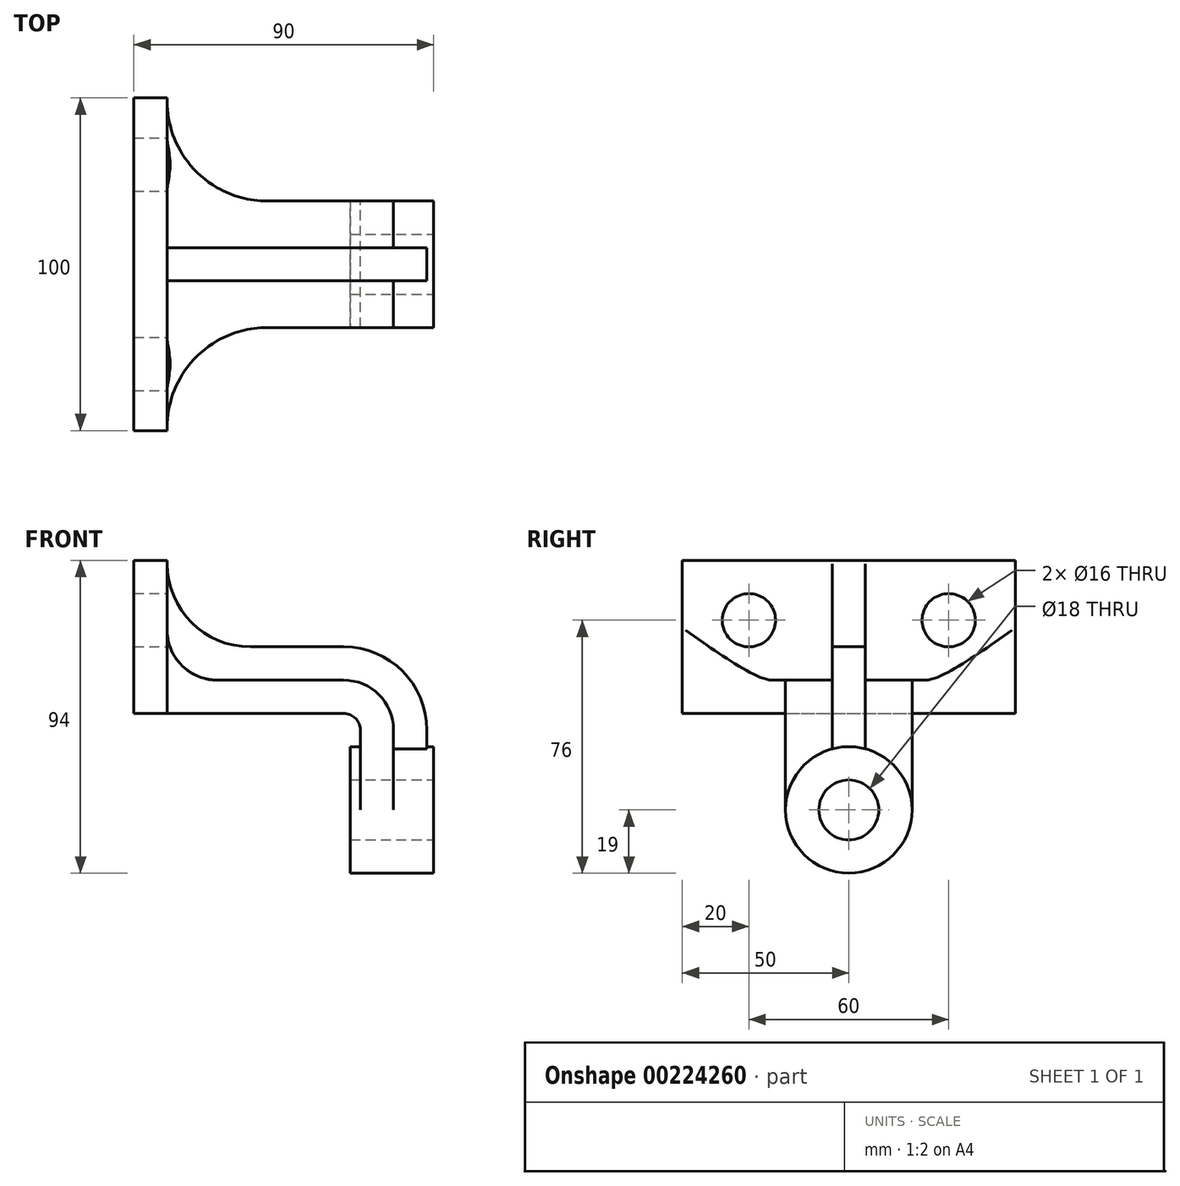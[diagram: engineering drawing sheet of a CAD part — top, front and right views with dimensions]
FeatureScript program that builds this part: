
annotation { "Feature Type Name" : "Feature", "Feature Type Description" : "" }
export const myFeature = defineFeature(function(context is Context, id is Id, definition is map)
    precondition{}
    {
        {
            var Q0;
            Q0=qCreatedBy(makeId("Front.planeOp"),FACE);
            var sketch = newSketch(context, id + "F0", { "sketchPlane" : qUnion([Q0])});
            skLineSegment(sketch, "E0", {"start": v(0, 0) * mm, "end": v(0, 46) * mm});
            skLineSegment(sketch, "E1", {"start": v(0, 46) * mm, "end": v(10, 46) * mm});
            skLineSegment(sketch, "E2", {"start": v(10, 46) * mm, "end": v(10, 0) * mm});
            skLineSegment(sketch, "E3", {"start": v(10, 0) * mm, "end": v(0, 0) * mm});
            skLineSegment(sketch, "E4", {"start": v(0, 0) * mm, "end": v(0, 10) * mm});
            skLineSegment(sketch, "E5", {"start": v(0, 10) * mm, "end": v(78, 10) * mm});
            skLineSegment(sketch, "E6", {"start": v(78, 10) * mm, "end": v(78, 0) * mm});
            skLineSegment(sketch, "E7", {"start": v(78, 0) * mm, "end": v(0, 0) * mm});
            skLineSegment(sketch, "E8", {"start": v(78, 10) * mm, "end": v(78, -48) * mm});
            skLineSegment(sketch, "E9", {"start": v(78, -48) * mm, "end": v(68, -48) * mm});
            skLineSegment(sketch, "E10", {"start": v(68, -48) * mm, "end": v(68, 10) * mm});
            skSolve(sketch);
        }
        {
            var Q0;
            {var subQ0=sQuery(id+"F0.wireOp",EDGE,"E0");Q0=makeQuery(id+"F0.imprint","IMPRINT",FACE,{"disambiguationData":[TD([[makeQuery(id+"F0.imprint","IMPRINT",EDGE,{"derivedFrom":subQ0}),-1.0]])]});}
            var Q1;
            {var subQ5=sQuery(id+"F0.wireOp",EDGE,"E4");Q1=makeQuery(id+"F0.imprint","IMPRINT",FACE,{"disambiguationData":[TD([[makeQuery(id+"F0.imprint","IMPRINT",EDGE,{"derivedFrom":subQ5}),-1.0]])]});}
            var Q2;
            {var subQ0=sQuery(id+"F0.wireOp",EDGE,"E7");var subQ1=sQuery(id+"F0.wireOp",EDGE,"E2");var subQ2=makeQuery(id+"F0.imprint","INTERSECT",VERTEX,{"derivedFrom":[subQ1,subQ0]});Q2=makeQuery(id+"F0.imprint","IMPRINT",FACE,{"disambiguationData":[TD([[makeQuery(id+"F0.imprint","IMPRINT",EDGE,{"disambiguationData":[TD([[subQ2,1.0]])],"derivedFrom":subQ1}),1.0]])]});}
            var Q3;
            {var subQ0=sQuery(id+"F0.wireOp",EDGE,"E8");var subQ1=sQuery(id+"F0.wireOp",EDGE,"E5");var subQ2=makeQuery(id+"F0.imprint","INTERSECT",VERTEX,{"derivedFrom":[subQ1,subQ0]});Q3=makeQuery(id+"F0.imprint","IMPRINT",FACE,{"disambiguationData":[TD([[makeQuery(id+"F0.imprint","IMPRINT",EDGE,{"disambiguationData":[TD([[subQ2,1.0]])],"derivedFrom":subQ1}),-1.0]])]});}
            var Q4;
            {var subQ5=sQuery(id+"F0.wireOp",EDGE,"E9");Q4=makeQuery(id+"F0.imprint","IMPRINT",FACE,{"disambiguationData":[TD([[makeQuery(id+"F0.imprint","IMPRINT",EDGE,{"derivedFrom":subQ5}),-1.0]])]});}
            extrude(context, id + "F1", {"entities" : qUnion([Q0, Q1, Q2, Q3, Q4]), "endBound" : BoundingType.SYMMETRIC, "depth" : 100 * mm});
        }
        {
            var Q0;
            Q0=makeQuery(id+"F1.opExtrude","SWEPT_FACE",FACE,{"disambiguationData":[OSD([sQuery(id+"F0.wireOp",EDGE,"E2")])]});
            var sketch = newSketch(context, id + "F2", { "sketchPlane" : qUnion([Q0])});
            skCircle(sketch, "E11", {"center": v(-30, 28) * mm, "radius": 8 * mm});
            skCircle(sketch, "E12", {"center": v(30, 28) * mm, "radius": 8 * mm});
            skSolve(sketch);
        }
        {
            var Q0;
            Q0=makeQuery(id+"F1.opExtrude","SWEPT_FACE",FACE,{"disambiguationData":[OSD([sQuery(id+"F0.wireOp",EDGE,"E5")])]});
            var sketch = newSketch(context, id + "F3", { "sketchPlane" : qUnion([Q0])});
            skLineSegment(sketch, "E13", {"start": v(10, -19) * mm, "end": v(78, -19) * mm});
            skLineSegment(sketch, "E14", {"start": v(10, 19) * mm, "end": v(78, 19) * mm});
            skArc(sketch, "E15", {"start": v(40, -19) * mm, "mid": v(18.79, -27.79) * mm, "end": v(10, -49) * mm});
            skArc(sketch, "E16", {"start": v(10, 49) * mm, "mid": v(18.79, 27.79) * mm, "end": v(40, 19) * mm});
            skLineSegment(sketch, "E17.0", {"start": v(10, -22) * mm, "end": v(10, -38) * mm});
            skLineSegment(sketch, "E18.0", {"start": v(10, 38) * mm, "end": v(10, 22) * mm});
            skLineSegment(sketch, "E19.0", {"start": v(10, -50) * mm, "end": v(10, 50) * mm});
            skSolve(sketch);
        }
        {
            var Q0;
            {var subQ3=sQuery(id+"F3.wireOp",EDGE,"E15");Q0=makeQuery(id+"F3.imprint","IMPRINT",FACE,{"disambiguationData":[TD([[makeQuery(id+"F3.imprint","IMPRINT",EDGE,{"derivedFrom":subQ3}),1.0]])]});}
            var Q1;
            {var subQ3=sQuery(id+"F3.wireOp",EDGE,"E16");Q1=makeQuery(id+"F3.imprint","IMPRINT",FACE,{"disambiguationData":[TD([[makeQuery(id+"F3.imprint","IMPRINT",EDGE,{"derivedFrom":subQ3}),1.0]])]});}
            extrude(context, id + "F4", {"entities" : qUnion([Q0, Q1]), "operationType" : NewBodyOperationType.REMOVE, "endBound" : BoundingType.THROUGH_ALL, "oppositeDirection" : true, "depth" : 25 * mm});
        }
        {
            var Q0;
            Q0=makeQuery(id+"F2.imprint","IMPRINT",FACE,{"disambiguationData":[TD([[makeQuery(id+"F2.imprint","IMPRINT",EDGE,{"derivedFrom":sQuery(id+"F2.wireOp",EDGE,"E12")}),1.0]])]});
            var Q1;
            Q1=makeQuery(id+"F2.imprint","IMPRINT",FACE,{"disambiguationData":[TD([[makeQuery(id+"F2.imprint","IMPRINT",EDGE,{"derivedFrom":sQuery(id+"F2.wireOp",EDGE,"E11")}),1.0]])]});
            extrude(context, id + "F5", {"entities" : qUnion([Q0, Q1]), "operationType" : NewBodyOperationType.REMOVE, "oppositeDirection" : true, "depth" : 25 * mm});
        }
        {
            var Q0;
            Q0=makeQuery(id+"F1.opExtrude","SWEPT_EDGE",EDGE,{"disambiguationData":[OSD([sQuery(id+"F0.wireOp",EDGE,"E5"),sQuery(id+"F0.wireOp",EDGE,"E8")])]});
            fillet(context, id + "F6", {"entities" : qUnion([Q0]), "radius" : 15 * mm, "tangentPropagation" : true, "allowEdgeOverflow" : false});
        }
        {
            var Q0;
            Q0=makeQuery(id+"F1.opExtrude","SWEPT_EDGE",EDGE,{"disambiguationData":[OSD([sQuery(id+"F0.wireOp",EDGE,"E7"),sQuery(id+"F0.wireOp",EDGE,"E10")])]});
            fillet(context, id + "F7", {"entities" : qUnion([Q0]), "radius" : 5 * mm, "tangentPropagation" : true, "allowEdgeOverflow" : false});
        }
        {
            var Q0;
            Q0=qCreatedBy(makeId("Front.planeOp"),FACE);
            var sketch = newSketch(context, id + "F8", { "sketchPlane" : qUnion([Q0])});
            skLineSegment(sketch, "E20.0", {"start": v(10, 46) * mm, "end": v(10, 0) * mm});
            skLineSegment(sketch, "E21", {"start": v(35, 20) * mm, "end": v(88, 20) * mm});
            skLineSegment(sketch, "E22", {"start": v(88, 20) * mm, "end": v(88, -48) * mm});
            skLineSegment(sketch, "E23", {"start": v(88, -48) * mm, "end": v(77.42, -48) * mm});
            skArc(sketch, "E24", {"start": v(10, 45) * mm, "mid": v(17.32, 27.32) * mm, "end": v(35, 20) * mm});
            skLineSegment(sketch, "E25.0.0", {"start": v(0, 0) * mm, "end": v(10, 0) * mm});
            skLineSegment(sketch, "E25.0.1", {"start": v(10, 0) * mm, "end": v(10, 46) * mm});
            skLineSegment(sketch, "E25.0.2", {"start": v(10, 46) * mm, "end": v(0, 46) * mm});
            skLineSegment(sketch, "E25.0.3", {"start": v(0, 46) * mm, "end": v(0, 0) * mm});
            skLineSegment(sketch, "E26.0", {"start": v(10, 10) * mm, "end": v(40, 10) * mm});
            skLineSegment(sketch, "E27.0", {"start": v(10, 10) * mm, "end": v(63, 10) * mm});
            skArc(sketch, "E28.0", {"start": v(78, -5) * mm, "mid": v(73.6, 5.6) * mm, "end": v(63, 10) * mm});
            skLineSegment(sketch, "E29.0", {"start": v(78, -48) * mm, "end": v(78, -5) * mm});
            skPoint(sketch, "E30.orphan", {"position": v(78, 10) * mm});
            skSolve(sketch);
        }
        {
            var Q0;
            Q0=makeQuery(id+"F8.imprint","IMPRINT",FACE,{"disambiguationData":[TD([[makeQuery(id+"F8.imprint","IMPRINT",EDGE,{"derivedFrom":sQuery(id+"F8.wireOp",EDGE,"E21")}),-1.0]])]});
            extrude(context, id + "F9", {"entities" : qUnion([Q0]), "operationType" : NewBodyOperationType.ADD, "endBound" : BoundingType.SYMMETRIC, "depth" : 10 * mm});
        }
        {
            var Q0;
            Q0=makeQuery(id+"F9.opExtrude","SWEPT_EDGE",EDGE,{"disambiguationData":[OSD([sQuery(id+"F8.wireOp",EDGE,"E21"),sQuery(id+"F8.wireOp",EDGE,"E22")])]});
            fillet(context, id + "F10", {"entities" : qUnion([Q0]), "radius" : 25 * mm, "tangentPropagation" : true, "allowEdgeOverflow" : false});
        }
        {
            var Q0;
            Q0=makeQuery(id+"F9.opExtrude","SWEPT_FACE",FACE,{"disambiguationData":[OSD([sQuery(id+"F8.wireOp",EDGE,"E22")])]});
            cPlane(context, id + "F11", {"entities" : qUnion([Q0]), "cplaneType" : CPlaneType.OFFSET, "offset" : 2 * mm, "width" : 150 * mm, "height" : 150 * mm});
        }
        {
            var Q0;
            Q0=qCreatedBy(id+"F11.planeOp",FACE);
            var sketch = newSketch(context, id + "F12", { "sketchPlane" : qUnion([Q0])});
            skCircle(sketch, "E31", {"center": v(0, -29) * mm, "radius": 19 * mm});
            skCircle(sketch, "E32", {"center": v(0, -29) * mm, "radius": 9 * mm});
            skLineSegment(sketch, "E33.0", {"start": v(-19, -48) * mm, "end": v(-5, -48) * mm});
            skLineSegment(sketch, "E34.0", {"start": v(-5, -48) * mm, "end": v(5, -48) * mm});
            skLineSegment(sketch, "E35.0", {"start": v(5, -48) * mm, "end": v(19, -48) * mm});
            skLineSegment(sketch, "E36.0", {"start": v(19, -48) * mm, "end": v(19, -5) * mm});
            skLineSegment(sketch, "E37.0", {"start": v(-19, -48) * mm, "end": v(-19, -5) * mm});
            skSolve(sketch);
        }
        {
            var Q0;
            {var subQ5=sQuery(id+"F12.wireOp",EDGE,"E33.0");Q0=makeQuery(id+"F12.imprint","IMPRINT",FACE,{"disambiguationData":[TD([[makeQuery(id+"F12.imprint","IMPRINT",EDGE,{"derivedFrom":subQ5}),1.0]])]});}
            var Q1;
            {var subQ5=sQuery(id+"F12.wireOp",EDGE,"E35.0");Q1=makeQuery(id+"F12.imprint","IMPRINT",FACE,{"disambiguationData":[TD([[makeQuery(id+"F12.imprint","IMPRINT",EDGE,{"derivedFrom":subQ5}),1.0]])]});}
            extrude(context, id + "F13", {"entities" : qUnion([Q0, Q1]), "operationType" : NewBodyOperationType.REMOVE, "oppositeDirection" : true, "depth" : 25 * mm});
        }
        {
            var Q0;
            Q0=makeQuery(id+"F12.imprint","IMPRINT",FACE,{"disambiguationData":[TD([[makeQuery(id+"F12.imprint","IMPRINT",EDGE,{"derivedFrom":sQuery(id+"F12.wireOp",EDGE,"E32")}),-1.0]])]});
            extrude(context, id + "F14", {"entities" : qUnion([Q0]), "operationType" : NewBodyOperationType.ADD, "oppositeDirection" : true, "depth" : 25 * mm});
        }
        {
            var Q0;
            Q0=makeQuery(id+"F12.imprint","IMPRINT",FACE,{"disambiguationData":[TD([[makeQuery(id+"F12.imprint","IMPRINT",EDGE,{"derivedFrom":sQuery(id+"F12.wireOp",EDGE,"E32")}),1.0]])]});
            extrude(context, id + "F15", {"entities" : qUnion([Q0]), "operationType" : NewBodyOperationType.REMOVE, "oppositeDirection" : true, "depth" : 25 * mm});
        }
    });
